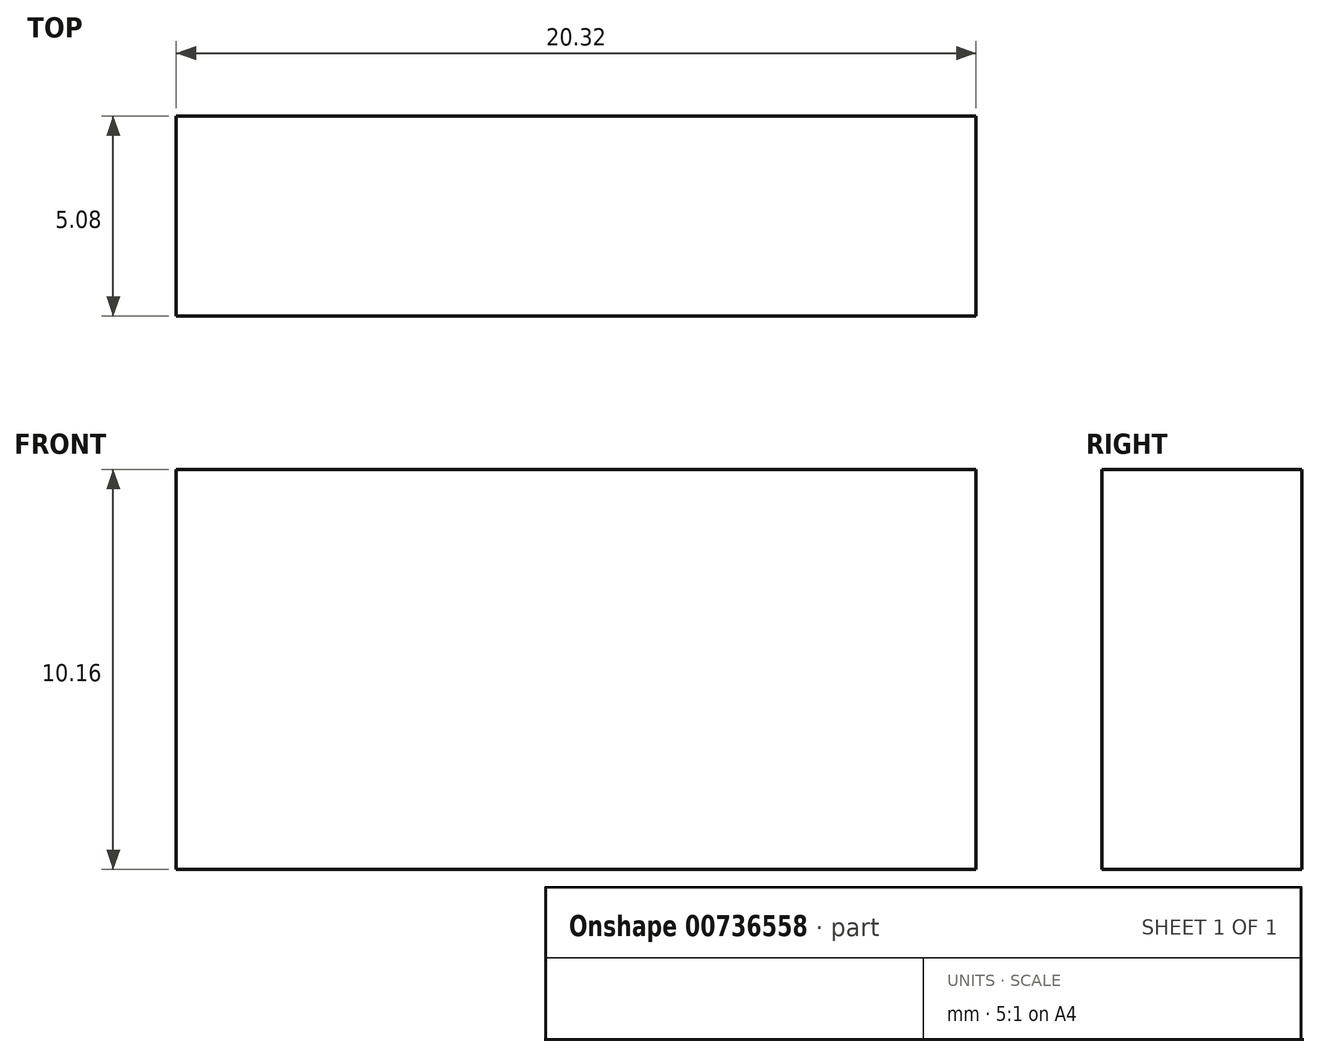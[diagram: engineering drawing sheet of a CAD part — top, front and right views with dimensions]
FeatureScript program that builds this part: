
annotation { "Feature Type Name" : "Feature", "Feature Type Description" : "" }
export const myFeature = defineFeature(function(context is Context, id is Id, definition is map)
    precondition{}
    {
        {
            var Q0;
            Q0=qCreatedBy(makeId("Front.planeOp"),FACE);
            var sketch = newSketch(context, id + "F0", { "sketchPlane" : qUnion([Q0])});
            skLineSegment(sketch, "E0.bottom", {"start": v(-8.07, 1.01) * mm, "end": v(12.25, 1.01) * mm});
            skLineSegment(sketch, "E0.top", {"start": v(-8.07, -9.15) * mm, "end": v(12.25, -9.15) * mm});
            skLineSegment(sketch, "E0.left", {"start": v(-8.07, 1.01) * mm, "end": v(-8.07, -9.15) * mm});
            skLineSegment(sketch, "E0.right", {"start": v(12.25, 1.01) * mm, "end": v(12.25, -9.15) * mm});
            skSolve(sketch);
        }
        {
            var Q0;
            Q0=makeQuery(id+"F0.imprint","IMPRINT",FACE,{"disambiguationData":[TD([[makeQuery(id+"F0.imprint","IMPRINT",EDGE,{"derivedFrom":sQuery(id+"F0.wireOp",EDGE,"E0.bottom")}),-1.0]])]});
            extrude(context, id + "F1", {"entities" : qUnion([Q0]), "depth" : 5.08 * mm, "offsetDistance" : 25.4 * mm});
        }
    });
